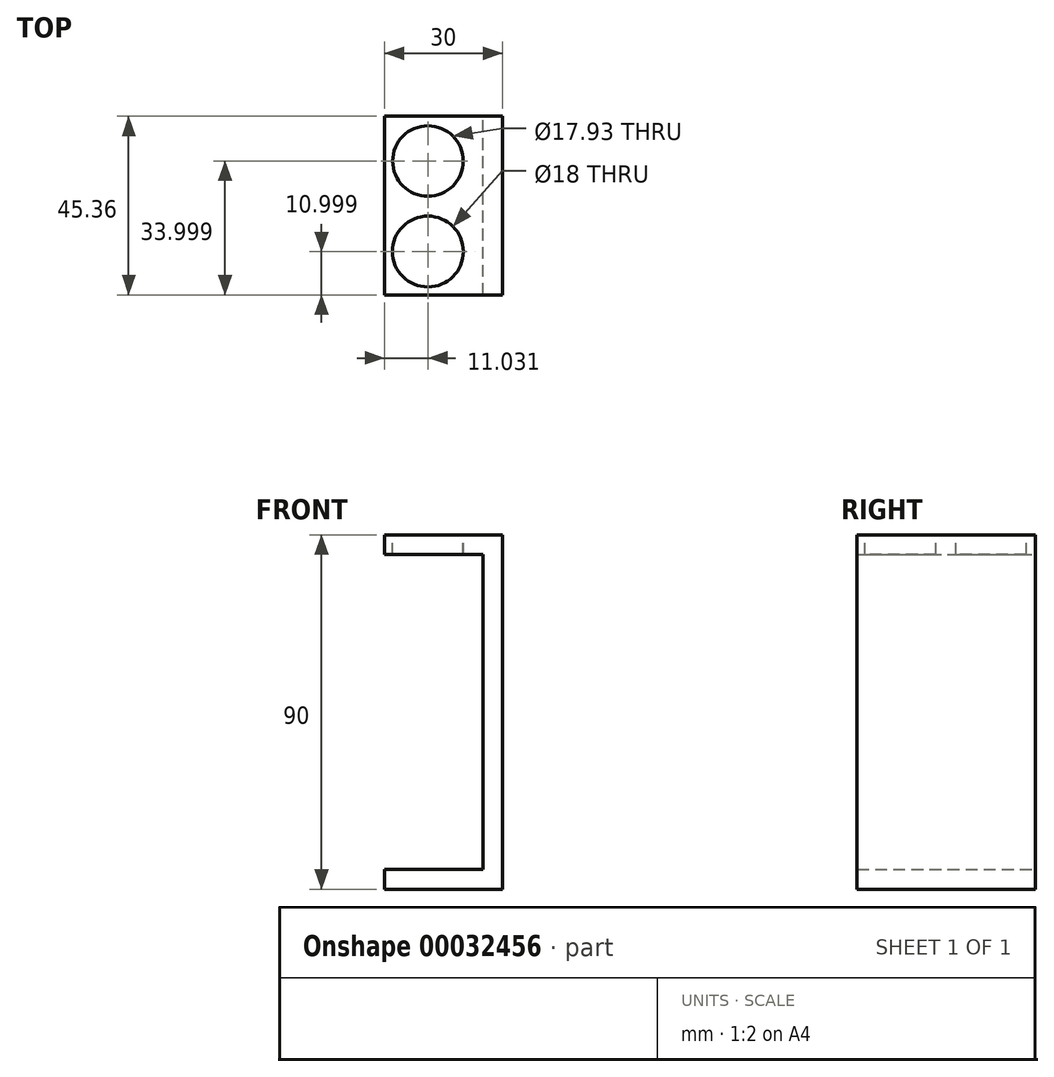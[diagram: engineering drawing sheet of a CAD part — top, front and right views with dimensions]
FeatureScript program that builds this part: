
annotation { "Feature Type Name" : "Feature", "Feature Type Description" : "" }
export const myFeature = defineFeature(function(context is Context, id is Id, definition is map)
    precondition{}
    {
        {
            var Q0;
            Q0=qCreatedBy(makeId("Front.planeOp"),FACE);
            var sketch = newSketch(context, id + "F0", { "sketchPlane" : qUnion([Q0])});
            skLineSegment(sketch, "E0.bottom", {"start": v(-40.35, 43.27) * mm, "end": v(33.12, 43.27) * mm});
            skLineSegment(sketch, "E0.top", {"start": v(-40.35, -58.02) * mm, "end": v(33.12, -58.02) * mm});
            skLineSegment(sketch, "E0.left", {"start": v(-40.35, 43.27) * mm, "end": v(-40.35, -58.02) * mm});
            skLineSegment(sketch, "E0.right", {"start": v(33.12, 43.27) * mm, "end": v(33.12, -58.02) * mm});
            skSolve(sketch);
        }
        {
            var Q0;
            Q0=qCreatedBy(makeId("Front.planeOp"),FACE);
            var sketch = newSketch(context, id + "F1", { "sketchPlane" : qUnion([Q0])});
            skLineSegment(sketch, "E1", {"start": v(-15.14, 3.73) * mm, "end": v(9.86, 3.73) * mm});
            skLineSegment(sketch, "E2", {"start": v(9.86, 3.73) * mm, "end": v(9.86, -76.27) * mm});
            skLineSegment(sketch, "E3", {"start": v(9.86, -76.27) * mm, "end": v(-15.08, -76.27) * mm});
            skLineSegment(sketch, "E4", {"start": v(-15.14, 3.73) * mm, "end": v(-15.14, 8.73) * mm});
            skLineSegment(sketch, "E5", {"start": v(-15.14, 8.73) * mm, "end": v(14.86, 8.73) * mm});
            skLineSegment(sketch, "E6", {"start": v(14.86, 8.73) * mm, "end": v(14.86, -81.27) * mm});
            skLineSegment(sketch, "E7", {"start": v(14.86, -81.27) * mm, "end": v(-15.14, -81.27) * mm});
            skLineSegment(sketch, "E8", {"start": v(-15.14, -81.27) * mm, "end": v(-15.08, -76.27) * mm});
            skSolve(sketch);
        }
        {
            var Q0;
            Q0 = qSketchRegion(id + "F1", true);
            extrude(context, id + "F2", {"entities" : qUnion([Q0]), "depth" : 45.36 * mm});
        }
        {
            var Q0;
            Q0=makeQuery(id+"F2.opExtrude","SWEPT_FACE",FACE,{"disambiguationData":[OSD([sQuery(id+"F1.wireOp",EDGE,"E5")])]});
            var sketch = newSketch(context, id + "F3", { "sketchPlane" : qUnion([Q0])});
            skCircle(sketch, "E9", {"center": v(-4.1, -34.36) * mm, "radius": 9 * mm});
            skCircle(sketch, "E10", {"center": v(-4.1, -11.36) * mm, "radius": 8.96 * mm});
            skSolve(sketch);
        }
        {
            var Q0;
            Q0 = qSketchRegion(id + "F3", true);
            extrude(context, id + "F4", {"entities" : qUnion([Q0]), "operationType" : NewBodyOperationType.REMOVE, "oppositeDirection" : true, "depth" : 59.16 * mm});
        }
    });
